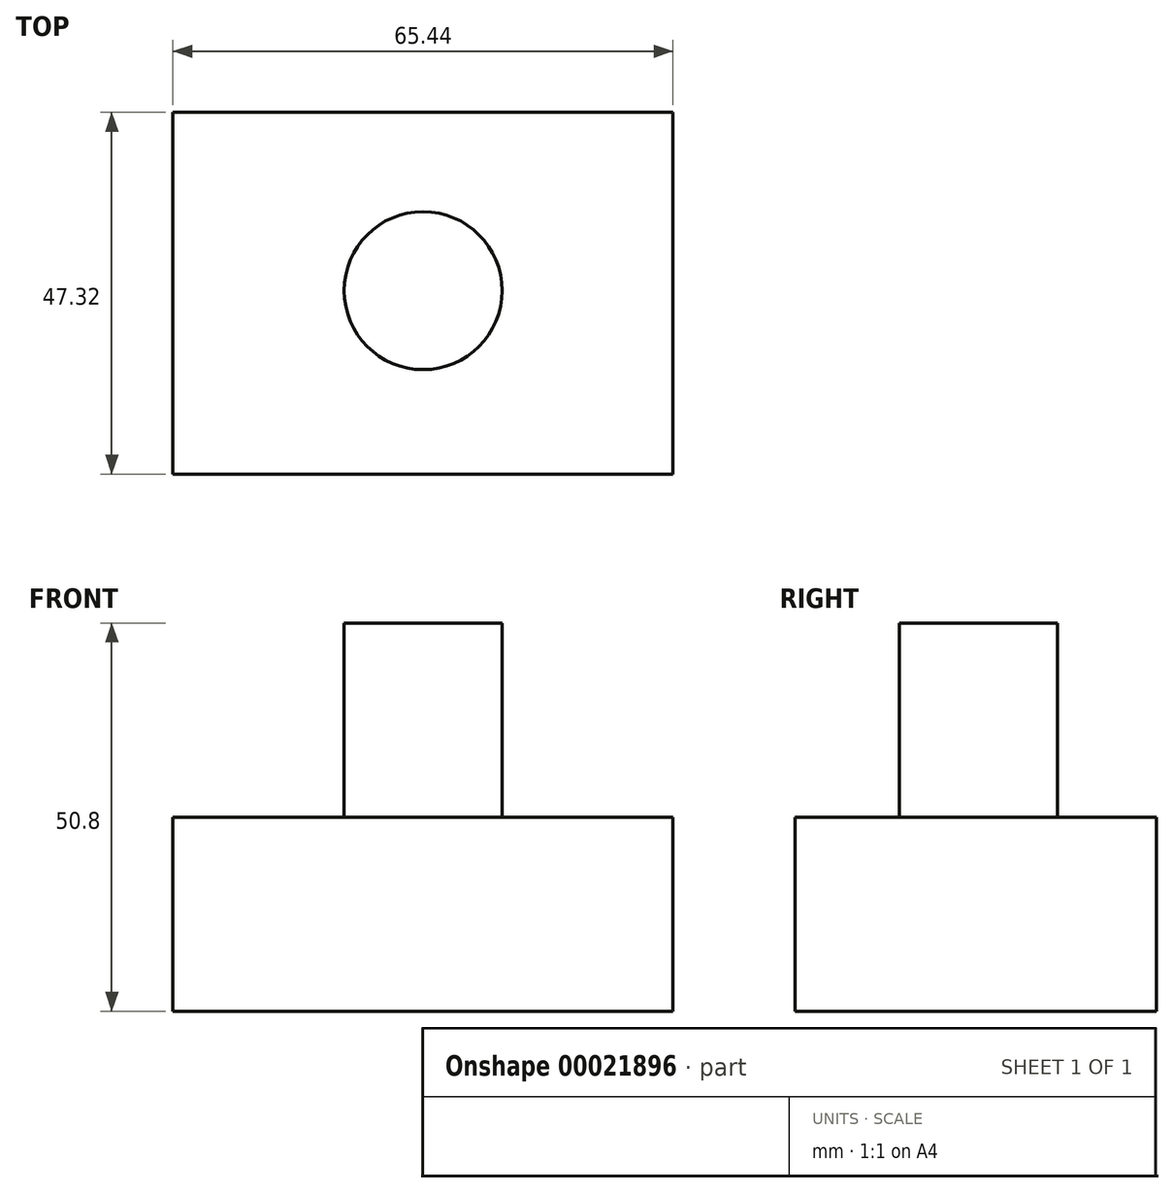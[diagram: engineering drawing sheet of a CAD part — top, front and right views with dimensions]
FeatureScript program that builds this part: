
annotation { "Feature Type Name" : "Feature", "Feature Type Description" : "" }
export const myFeature = defineFeature(function(context is Context, id is Id, definition is map)
    precondition{}
    {
        {
            var Q0;
            Q0=qCreatedBy(makeId("Top.planeOp"),FACE);
            var sketch = newSketch(context, id + "F0", { "sketchPlane" : qUnion([Q0])});
            skLineSegment(sketch, "E0.bottom", {"start": v(0, 0) * mm, "end": v(65.44, 0) * mm});
            skLineSegment(sketch, "E0.top", {"start": v(0, -47.32) * mm, "end": v(65.44, -47.32) * mm});
            skLineSegment(sketch, "E0.left", {"start": v(0, 0) * mm, "end": v(0, -47.32) * mm});
            skLineSegment(sketch, "E0.right", {"start": v(65.44, 0) * mm, "end": v(65.44, -47.32) * mm});
            skSolve(sketch);
        }
        {
            var Q0;
            Q0=makeQuery(id+"F0.imprint","IMPRINT",FACE,{"disambiguationData":[TD([[makeQuery(id+"F0.imprint","IMPRINT",EDGE,{"derivedFrom":sQuery(id+"F0.wireOp",EDGE,"E0.bottom")}),-1.0]])]});
            extrude(context, id + "F1", {"entities" : qUnion([Q0]), "depth" : 25.4 * mm});
        }
        {
            var Q0;
            Q0=makeQuery(id+"F1.opExtrude","CAP_FACE",FACE,{"disambiguationData":[OSD([sQuery(id+"F0.wireOp",EDGE,"E0.bottom"),sQuery(id+"F0.wireOp",EDGE,"E0.top"),sQuery(id+"F0.wireOp",EDGE,"E0.left"),sQuery(id+"F0.wireOp",EDGE,"E0.right")])],"isStart":false});
            var sketch = newSketch(context, id + "F2", { "sketchPlane" : qUnion([Q0])});
            skCircle(sketch, "E1", {"center": v(32.75, -23.32) * mm, "radius": 10.34 * mm});
            skSolve(sketch);
        }
        {
            var Q0;
            Q0 = qSketchRegion(id + "F2", true);
            extrude(context, id + "F3", {"entities" : qUnion([Q0]), "operationType" : NewBodyOperationType.ADD, "depth" : 25.4 * mm});
        }
    });
